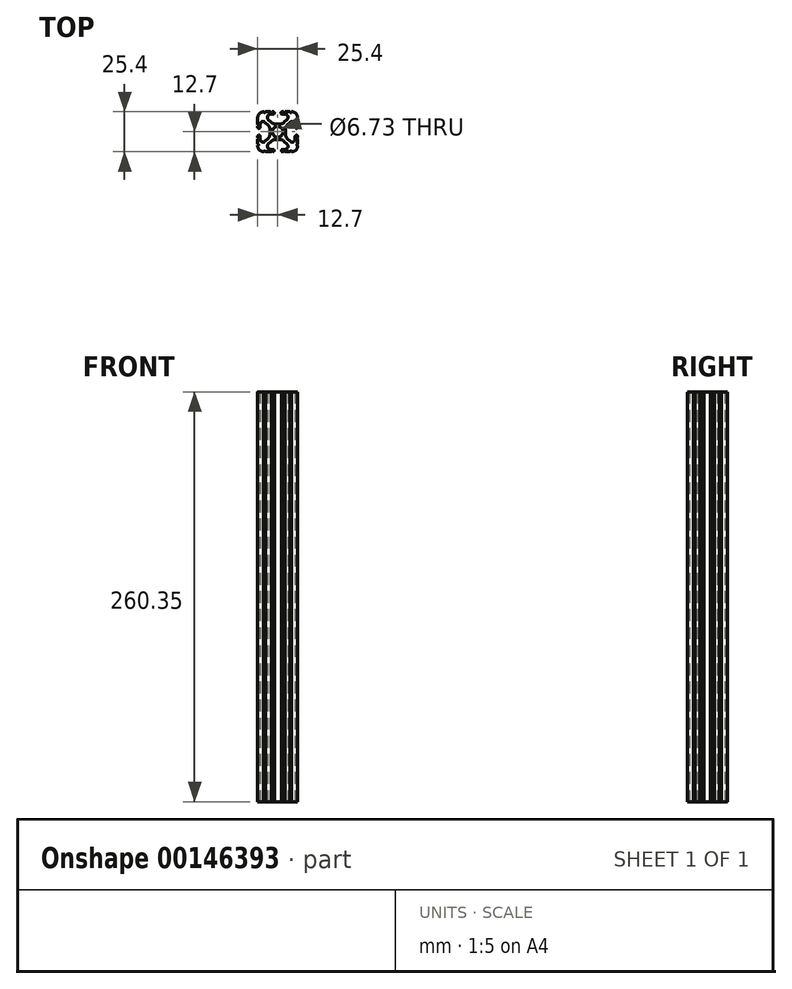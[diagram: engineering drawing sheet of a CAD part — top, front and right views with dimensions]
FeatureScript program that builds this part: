
annotation { "Feature Type Name" : "Feature", "Feature Type Description" : "" }
export const myFeature = defineFeature(function(context is Context, id is Id, definition is map)
    precondition{}
    {
        {
            var Q0;
            Q0=qCreatedBy(makeId("Top.planeOp"),FACE);
            var sketch = newSketch(context, id + "F0", { "sketchPlane" : qUnion([Q0])});
            skCircle(sketch, "E0", {"center": v(-12.7, 12.7) * mm, "radius": 3.36 * mm});
            skLineSegment(sketch, "E1.bottom", {"start": v(-11.24, 17.64) * mm, "end": v(-14.16, 17.64) * mm});
            skLineSegment(sketch, "E1.top", {"start": v(-11.24, 7.76) * mm, "end": v(-14.16, 7.76) * mm});
            skLineSegment(sketch, "E1.left", {"start": v(-7.76, 14.16) * mm, "end": v(-7.76, 11.24) * mm});
            skLineSegment(sketch, "E1.right", {"start": v(-17.64, 14.16) * mm, "end": v(-17.64, 11.24) * mm});
            skPoint(sketch, "E2.visualSharp", {"position": v(-25.4, 25.4) * mm});
            skPoint(sketch, "E3.visualSharp", {"position": v(0, 25.4) * mm});
            skPoint(sketch, "E4.visualSharp", {"position": v(0, 0) * mm});
            skPoint(sketch, "E5.visualSharp", {"position": v(-25.4, 0) * mm});
            skLineSegment(sketch, "E6.0", {"start": v(-18.7, 20.6) * mm, "end": v(-16.85, 18.76) * mm});
            skLineSegment(sketch, "E7.0", {"start": v(-20.6, 18.7) * mm, "end": v(-18.76, 16.85) * mm});
            skPoint(sketch, "E8.orphan", {"position": v(-23.85, 1.55) * mm});
            skPoint(sketch, "E9.orphan", {"position": v(-23.85, 23.85) * mm});
            skPoint(sketch, "E10.orphan", {"position": v(-1.55, 23.85) * mm});
            skPoint(sketch, "E11.orphan", {"position": v(-1.55, 1.55) * mm});
            skLineSegment(sketch, "E12", {"start": v(-8.55, 6.64) * mm, "end": v(-6.7, 4.8) * mm});
            skLineSegment(sketch, "E13.0", {"start": v(-18.7, 4.8) * mm, "end": v(-16.85, 6.64) * mm});
            skLineSegment(sketch, "E14.0", {"start": v(-20.6, 6.7) * mm, "end": v(-18.76, 8.55) * mm});
            skLineSegment(sketch, "E15.0", {"start": v(-8.55, 18.76) * mm, "end": v(-6.7, 20.6) * mm});
            skPoint(sketch, "E16.visualSharp", {"position": v(-23.85, 21.95) * mm});
            skArc(sketch, "E16.filletArc", {"start": v(-20.6, 18.7) * mm, "mid": v(-22.68, 19.1) * mm, "end": v(-23.85, 17.35) * mm});
            skPoint(sketch, "E17.visualSharp", {"position": v(-21.95, 23.85) * mm});
            skArc(sketch, "E17.filletArc", {"start": v(-17.35, 23.85) * mm, "mid": v(-19.1, 22.68) * mm, "end": v(-18.7, 20.6) * mm});
            skPoint(sketch, "E18.visualSharp", {"position": v(-5.34, 23.85) * mm});
            skLineSegment(sketch, "E19", {"start": v(-17.35, 23.85) * mm, "end": v(-15.58, 23.85) * mm});
            skLineSegment(sketch, "E20", {"start": v(-23.85, 17.35) * mm, "end": v(-23.85, 15.62) * mm});
            skLineSegment(sketch, "E21", {"start": v(-8.05, 1.55) * mm, "end": v(-9.78, 1.55) * mm});
            skArc(sketch, "E22.filletArc", {"start": v(-6.7, 20.6) * mm, "mid": v(-6.3, 22.68) * mm, "end": v(-8.05, 23.85) * mm});
            skPoint(sketch, "E23.visualSharp", {"position": v(-1.55, 3.45) * mm});
            skPoint(sketch, "E24.visualSharp", {"position": v(-3.45, 1.55) * mm});
            skArc(sketch, "E24.filletArc", {"start": v(-8.05, 1.55) * mm, "mid": v(-6.3, 2.73) * mm, "end": v(-6.7, 4.8) * mm});
            skArc(sketch, "E25.filletArc", {"start": v(-18.7, 4.8) * mm, "mid": v(-19.1, 2.73) * mm, "end": v(-17.35, 1.55) * mm});
            skArc(sketch, "E26.filletArc", {"start": v(-23.85, 8.05) * mm, "mid": v(-22.68, 6.3) * mm, "end": v(-20.6, 6.7) * mm});
            skLineSegment(sketch, "E27.bottom", {"start": v(-4.9, 0) * mm, "end": v(-8.05, 0) * mm});
            skLineSegment(sketch, "E27.top", {"start": v(-4.92, 25.4) * mm, "end": v(-8.05, 25.4) * mm});
            skLineSegment(sketch, "E27.left", {"start": v(0, 4.9) * mm, "end": v(0, 8.05) * mm});
            skLineSegment(sketch, "E27.right", {"start": v(-25.4, 4.9) * mm, "end": v(-25.4, 8.05) * mm});
            skArc(sketch, "E28.filletArc", {"start": v(-25.4, 3.81) * mm, "mid": v(-24.28, 1.12) * mm, "end": v(-21.59, 0) * mm});
            skArc(sketch, "E29.filletArc", {"start": v(-3.81, 0) * mm, "mid": v(-1.12, 1.12) * mm, "end": v(0, 3.8) * mm});
            skArc(sketch, "E30.filletArc", {"start": v(0, 21.59) * mm, "mid": v(-1.12, 24.28) * mm, "end": v(-3.8, 25.4) * mm});
            skArc(sketch, "E31.filletArc", {"start": v(-21.59, 25.4) * mm, "mid": v(-24.28, 24.28) * mm, "end": v(-25.4, 21.59) * mm});
            skPoint(sketch, "E32.newPointA", {"position": v(-17.64, 7.76) * mm});
            skArc(sketch, "E32.filletArc", {"start": v(-14.16, 7.76) * mm, "mid": v(-15.62, 7.47) * mm, "end": v(-16.85, 6.64) * mm});
            skPoint(sketch, "E33.newPointA", {"position": v(-7.76, 7.76) * mm});
            skArc(sketch, "E33.filletArc", {"start": v(-8.55, 6.64) * mm, "mid": v(-9.78, 7.47) * mm, "end": v(-11.24, 7.76) * mm});
            skArc(sketch, "E34.filletArc", {"start": v(-7.76, 11.24) * mm, "mid": v(-7.47, 9.78) * mm, "end": v(-6.64, 8.55) * mm});
            skArc(sketch, "E35.filletArc", {"start": v(-6.64, 16.85) * mm, "mid": v(-7.47, 15.62) * mm, "end": v(-7.76, 14.16) * mm});
            skPoint(sketch, "E36.newPointB", {"position": v(-7.76, 17.64) * mm});
            skArc(sketch, "E36.filletArc", {"start": v(-11.24, 17.64) * mm, "mid": v(-9.78, 17.93) * mm, "end": v(-8.55, 18.76) * mm});
            skPoint(sketch, "E37.newPointB", {"position": v(-17.64, 17.64) * mm});
            skArc(sketch, "E37.filletArc", {"start": v(-16.85, 18.76) * mm, "mid": v(-15.62, 17.93) * mm, "end": v(-14.16, 17.64) * mm});
            skArc(sketch, "E38.filletArc", {"start": v(-17.64, 14.16) * mm, "mid": v(-17.93, 15.62) * mm, "end": v(-18.76, 16.85) * mm});
            skArc(sketch, "E39.filletArc", {"start": v(-18.76, 8.55) * mm, "mid": v(-17.93, 9.78) * mm, "end": v(-17.64, 11.24) * mm});
            skLineSegment(sketch, "E40", {"start": v(-6.64, 8.55) * mm, "end": v(-4.8, 6.7) * mm});
            skPoint(sketch, "E41.visualSharp", {"position": v(-1.55, 21.95) * mm});
            skArc(sketch, "E42.filletArc", {"start": v(-4.8, 6.7) * mm, "mid": v(-2.73, 6.3) * mm, "end": v(-1.55, 8.05) * mm});
            skLineSegment(sketch, "E43", {"start": v(-1.55, 8.05) * mm, "end": v(-1.55, 9.78) * mm});
            skLineSegment(sketch, "E44", {"start": v(-6.64, 16.85) * mm, "end": v(-4.8, 18.7) * mm});
            skArc(sketch, "E45.filletArc", {"start": v(-1.55, 17.35) * mm, "mid": v(-2.73, 19.1) * mm, "end": v(-4.8, 18.7) * mm});
            skArc(sketch, "E46", {"start": v(-23.85, 9.78) * mm, "mid": v(-24.63, 10.56) * mm, "end": v(-25.4, 9.78) * mm});
            skArc(sketch, "E47", {"start": v(-25.4, 15.62) * mm, "mid": v(-24.63, 14.86) * mm, "end": v(-23.85, 15.62) * mm});
            skArc(sketch, "E48", {"start": v(-15.62, 23.85) * mm, "mid": v(-14.83, 24.63) * mm, "end": v(-15.62, 25.4) * mm});
            skArc(sketch, "E49", {"start": v(-9.78, 25.4) * mm, "mid": v(-10.6, 24.63) * mm, "end": v(-9.78, 23.85) * mm});
            skArc(sketch, "E50", {"start": v(-1.55, 15.62) * mm, "mid": v(-0.77, 14.88) * mm, "end": v(0, 15.62) * mm});
            skArc(sketch, "E51", {"start": v(0, 9.78) * mm, "mid": v(-0.77, 10.5) * mm, "end": v(-1.55, 9.78) * mm});
            skArc(sketch, "E52", {"start": v(-9.78, 1.55) * mm, "mid": v(-10.4, 0.77) * mm, "end": v(-9.78, 0) * mm});
            skArc(sketch, "E53", {"start": v(-15.62, 0) * mm, "mid": v(-14.85, 0.77) * mm, "end": v(-15.62, 1.55) * mm});
            skLineSegment(sketch, "E54.trimOffspring", {"start": v(-15.62, 1.55) * mm, "end": v(-17.35, 1.55) * mm});
            skLineSegment(sketch, "E55.trimOffspring", {"start": v(-16.7, 0) * mm, "end": v(-20.5, 0) * mm});
            skLineSegment(sketch, "E56.trimOffspring", {"start": v(-1.55, 15.62) * mm, "end": v(-1.55, 17.35) * mm});
            skLineSegment(sketch, "E57.trimOffspring", {"start": v(0, 15.62) * mm, "end": v(0, 16.26) * mm});
            skLineSegment(sketch, "E58.trimOffspring", {"start": v(-23.85, 9.78) * mm, "end": v(-23.85, 8.05) * mm});
            skLineSegment(sketch, "E59.trimOffspring", {"start": v(-25.4, 15.62) * mm, "end": v(-25.4, 16.26) * mm});
            skLineSegment(sketch, "E60.trimOffspring", {"start": v(-9.86, 23.85) * mm, "end": v(-8.05, 23.85) * mm});
            skLineSegment(sketch, "E61.trimOffspring", {"start": v(-15.58, 25.4) * mm, "end": v(-16.25, 25.4) * mm});
            skPoint(sketch, "E62.start.orphan", {"position": v(-15.62, 17.93) * mm});
            skPoint(sketch, "E63.start.orphan", {"position": v(-9.78, 17.93) * mm});
            skPoint(sketch, "E64.start.orphan", {"position": v(-7.47, 15.62) * mm});
            skPoint(sketch, "E65.start.orphan", {"position": v(-7.47, 9.78) * mm});
            skPoint(sketch, "E66.start.orphan", {"position": v(-17.93, 15.62) * mm});
            skPoint(sketch, "E67.start.orphan", {"position": v(-17.93, 9.78) * mm});
            skPoint(sketch, "E68.start.orphan", {"position": v(-9.78, 7.47) * mm});
            skPoint(sketch, "E69.start.orphan", {"position": v(-15.62, 7.47) * mm});
            skPoint(sketch, "E70.endSnap0", {"position": v(0, 18.6) * mm});
            skPoint(sketch, "E71.startSnap0", {"position": v(-1.55, 8.92) * mm});
            skArc(sketch, "E72", {"start": v(-4.92, 25.4) * mm, "mid": v(-4.37, 24.9) * mm, "end": v(-3.81, 25.4) * mm});
            skArc(sketch, "E73", {"start": v(-9.14, 25.4) * mm, "mid": v(-8.6, 24.86) * mm, "end": v(-8.05, 25.4) * mm});
            skArc(sketch, "E74", {"start": v(-17.35, 25.4) * mm, "mid": v(-16.8, 24.86) * mm, "end": v(-16.25, 25.4) * mm});
            skArc(sketch, "E75", {"start": v(-21.59, 25.4) * mm, "mid": v(-21.04, 24.85) * mm, "end": v(-20.49, 25.4) * mm});
            skLineSegment(sketch, "E76", {"start": v(-25.4, 21.59) * mm, "end": v(-25.4, 20.5) * mm});
            skArc(sketch, "E77", {"start": v(-25.4, 16.26) * mm, "mid": v(-24.84, 16.8) * mm, "end": v(-25.4, 17.35) * mm});
            skArc(sketch, "E78", {"start": v(-25.4, 8.05) * mm, "mid": v(-24.9, 8.6) * mm, "end": v(-25.4, 9.15) * mm});
            skArc(sketch, "E79", {"start": v(-25.4, 3.81) * mm, "mid": v(-24.85, 4.36) * mm, "end": v(-25.4, 4.9) * mm});
            skArc(sketch, "E80", {"start": v(-20.5, 0) * mm, "mid": v(-21.04, 0.55) * mm, "end": v(-21.59, 0) * mm});
            skArc(sketch, "E81", {"start": v(-15.62, 0) * mm, "mid": v(-16.16, 0.54) * mm, "end": v(-16.7, 0) * mm});
            skArc(sketch, "E82", {"start": v(-8.05, 0) * mm, "mid": v(-8.6, 0.55) * mm, "end": v(-9.15, 0) * mm});
            skArc(sketch, "E83", {"start": v(-3.81, 0) * mm, "mid": v(-4.35, 0.54) * mm, "end": v(-4.9, 0) * mm});
            skLineSegment(sketch, "E84.trimOffspring", {"start": v(-17.35, 25.4) * mm, "end": v(-20.49, 25.4) * mm});
            skLineSegment(sketch, "E85.trimOffspring", {"start": v(-25.4, 17.35) * mm, "end": v(-25.4, 21.59) * mm});
            skLineSegment(sketch, "E86.trimOffspring", {"start": v(-25.4, 9.15) * mm, "end": v(-25.4, 9.78) * mm});
            skLineSegment(sketch, "E87.trimOffspring", {"start": v(-9.15, 0) * mm, "end": v(-9.78, 0) * mm});
            skArc(sketch, "E88", {"start": v(0, 4.9) * mm, "mid": v(-0.54, 4.36) * mm, "end": v(0, 3.8) * mm});
            skArc(sketch, "E89", {"start": v(0, 9.15) * mm, "mid": v(-0.54, 8.6) * mm, "end": v(0, 8.05) * mm});
            skLineSegment(sketch, "E90.trimOffspring", {"start": v(0, 9.15) * mm, "end": v(0, 9.78) * mm});
            skArc(sketch, "E91", {"start": v(0, 21.59) * mm, "mid": v(-0.55, 21.04) * mm, "end": v(0, 20.5) * mm});
            skArc(sketch, "E92", {"start": v(0, 17.35) * mm, "mid": v(-0.55, 16.8) * mm, "end": v(0, 16.26) * mm});
            skLineSegment(sketch, "E93.trimOffspring", {"start": v(0, 17.35) * mm, "end": v(0, 20.5) * mm});
            skLineSegment(sketch, "E94.trimOffspring", {"start": v(-9.14, 25.4) * mm, "end": v(-9.86, 25.4) * mm});
            skSolve(sketch);
        }
        {
            var Q0;
            Q0=qSketchRegion(id+"F0",true);
            extrude(context, id + "F1", {"entities" : qUnion([Q0]), "depth" : 260.35 * mm});
        }
    });
